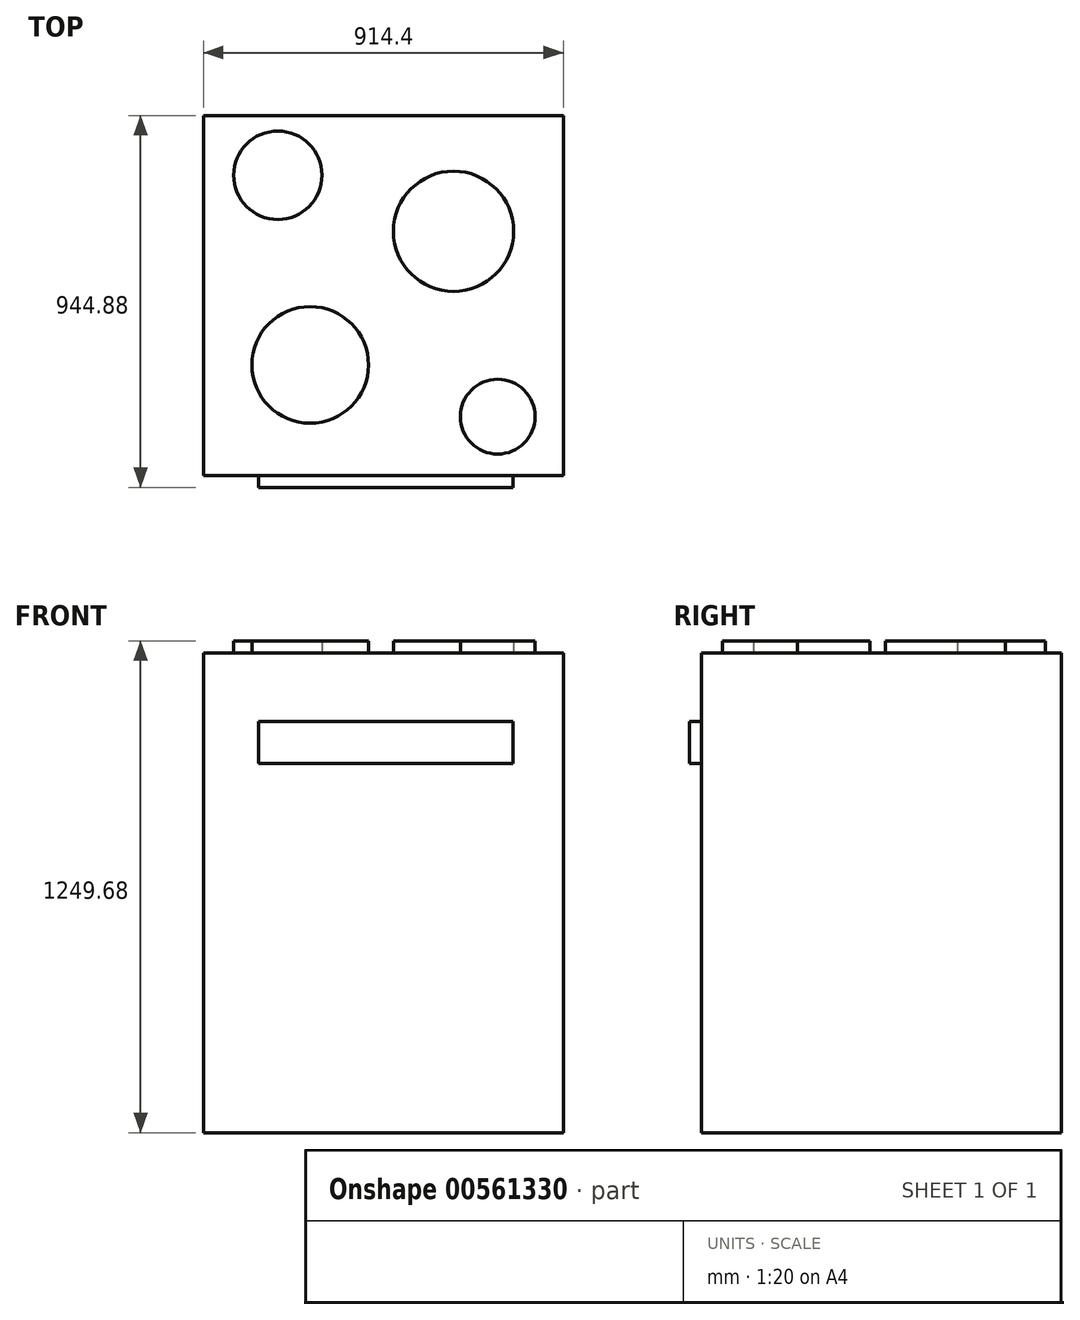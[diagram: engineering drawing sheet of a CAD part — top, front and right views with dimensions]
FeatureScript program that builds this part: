
annotation { "Feature Type Name" : "Feature", "Feature Type Description" : "" }
export const myFeature = defineFeature(function(context is Context, id is Id, definition is map)
    precondition{}
    {
        {
            var Q0;
            Q0=qCreatedBy(makeId("Top.planeOp"),FACE);
            var sketch = newSketch(context, id + "F0", { "sketchPlane" : qUnion([Q0])});
            skLineSegment(sketch, "E0.bottom", {"start": v(-452.8, 466.85) * mm, "end": v(461.6, 466.85) * mm});
            skLineSegment(sketch, "E0.top", {"start": v(-452.8, -447.55) * mm, "end": v(461.6, -447.55) * mm});
            skLineSegment(sketch, "E0.left", {"start": v(-452.8, 466.85) * mm, "end": v(-452.8, -447.55) * mm});
            skLineSegment(sketch, "E0.right", {"start": v(461.6, 466.85) * mm, "end": v(461.6, -447.55) * mm});
            skSolve(sketch);
        }
        {
            var Q0;
            Q0 = qSketchRegion(id + "F0", true);
            extrude(context, id + "F1", {"entities" : qUnion([Q0]), "depth" : 1219.2 * mm, "offsetDistance" : 30.48 * mm});
        }
        {
            var Q0;
            Q0=makeQuery(id+"F1.opExtrude","CAP_FACE",FACE,{"disambiguationData":[OSD([sQuery(id+"F0.wireOp",EDGE,"E0.bottom"),sQuery(id+"F0.wireOp",EDGE,"E0.top"),sQuery(id+"F0.wireOp",EDGE,"E0.left"),sQuery(id+"F0.wireOp",EDGE,"E0.right")])],"isStart":false});
            var sketch = newSketch(context, id + "F2", { "sketchPlane" : qUnion([Q0])});
            skCircle(sketch, "E1", {"center": v(-263.71, 314.84) * mm, "radius": 112.26 * mm});
            skCircle(sketch, "E2", {"center": v(294.85, -298.49) * mm, "radius": 94.93 * mm});
            skCircle(sketch, "E3", {"center": v(182.6, 172.46) * mm, "radius": 152.67 * mm});
            skCircle(sketch, "E4", {"center": v(-181.57, -167.06) * mm, "radius": 148.21 * mm});
            skSolve(sketch);
        }
        {
            var Q0;
            Q0 = qSketchRegion(id + "F2", true);
            extrude(context, id + "F3", {"entities" : qUnion([Q0]), "operationType" : NewBodyOperationType.ADD, "depth" : 30.48 * mm, "offsetDistance" : 30.48 * mm});
        }
        {
            var Q0;
            Q0=makeQuery(id+"F1.opExtrude","SWEPT_FACE",FACE,{"disambiguationData":[OSD([sQuery(id+"F0.wireOp",EDGE,"E0.top")])]});
            var sketch = newSketch(context, id + "F4", { "sketchPlane" : qUnion([Q0])});
            skLineSegment(sketch, "E5.bottom", {"start": v(-313, 1045.27) * mm, "end": v(333.19, 1045.27) * mm});
            skLineSegment(sketch, "E5.top", {"start": v(-313, 938.49) * mm, "end": v(333.19, 938.49) * mm});
            skLineSegment(sketch, "E5.left", {"start": v(-313, 1045.27) * mm, "end": v(-313, 938.49) * mm});
            skLineSegment(sketch, "E5.right", {"start": v(333.19, 1045.27) * mm, "end": v(333.19, 938.49) * mm});
            skSolve(sketch);
        }
        {
            var Q0;
            Q0 = qSketchRegion(id + "F4", true);
            extrude(context, id + "F5", {"entities" : qUnion([Q0]), "operationType" : NewBodyOperationType.ADD, "depth" : 30.48 * mm, "offsetDistance" : 30.48 * mm});
        }
    });
